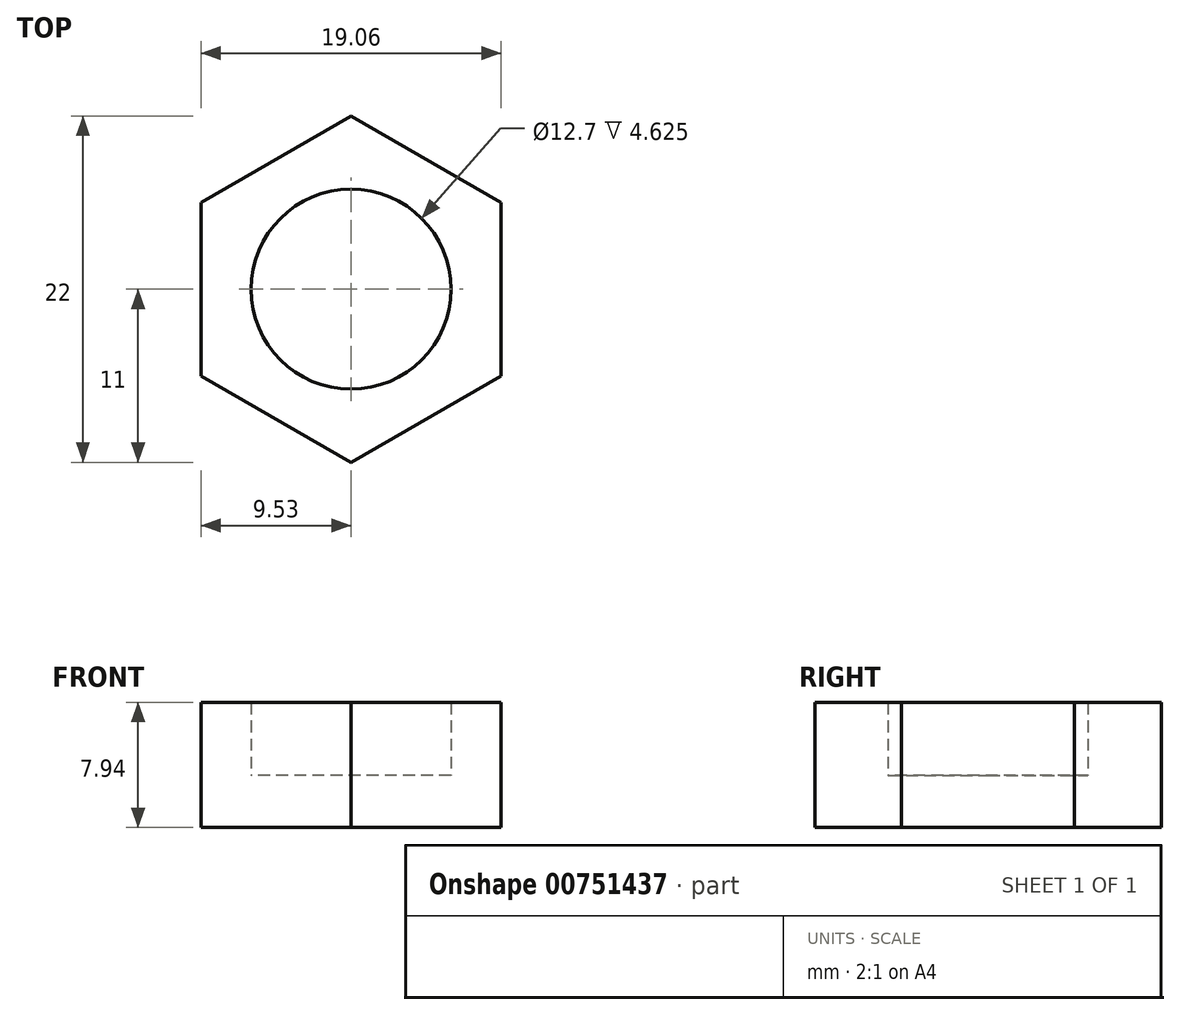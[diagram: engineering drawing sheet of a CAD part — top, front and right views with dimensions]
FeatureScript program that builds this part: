
annotation { "Feature Type Name" : "Feature", "Feature Type Description" : "" }
export const myFeature = defineFeature(function(context is Context, id is Id, definition is map)
    precondition{}
    {
        {
            assignVariable(context, id + "F0", {"name" : "ShaftHeight", "anyValue" : 3});
        }
        {
            var Q0;
            Q0=qCreatedBy(makeId("Top.planeOp"),FACE);
            var sketch = newSketch(context, id + "F1", { "sketchPlane" : qUnion([Q0])});
            skCircle(sketch, "E0.cCircle", {"center": v(0, 0) * mm, "radius": 9.53 * mm, "construction": true});
            skLineSegment(sketch, "E0.0", {"start": v(9.53, 5.5) * mm, "end": v(9.53, -5.5) * mm});
            skLineSegment(sketch, "E0.1", {"start": v(9.53, -5.5) * mm, "end": v(0, -11) * mm});
            skLineSegment(sketch, "E0.2", {"start": v(0, -11) * mm, "end": v(-9.52, -5.5) * mm});
            skLineSegment(sketch, "E0.3", {"start": v(-9.52, -5.5) * mm, "end": v(-9.53, 5.5) * mm});
            skLineSegment(sketch, "E0.4", {"start": v(-9.53, 5.5) * mm, "end": v(0, 11) * mm});
            skLineSegment(sketch, "E0.5", {"start": v(0, 11) * mm, "end": v(9.53, 5.5) * mm});
            skPoint(sketch, "E0.0.midPoint", {"position": v(9.53, 0) * mm});
            skCircle(sketch, "E1", {"center": v(0, 0) * mm, "radius": 6.35 * mm});
            skSolve(sketch);
        }
        {
            var Q0;
            Q0=makeQuery(id+"F1.imprint","IMPRINT",FACE,{"disambiguationData":[TD([[makeQuery(id+"F1.imprint","IMPRINT",EDGE,{"derivedFrom":sQuery(id+"F1.wireOp",EDGE,"E0.0")}),-1.0]])]});
            extrude(context, id + "F2", {"entities" : qUnion([Q0]), "depth" : 7.94 * mm, "offsetDistance" : 25.4 * mm});
        }
        {
            var Q0;
            Q0=makeQuery(id+"F1.imprint","IMPRINT",FACE,{"disambiguationData":[TD([[makeQuery(id+"F1.imprint","IMPRINT",EDGE,{"derivedFrom":sQuery(id+"F1.wireOp",EDGE,"E1")}),1.0]])]});
            extrude(context, id + "F3", {"entities" : qUnion([Q0]), "operationType" : NewBodyOperationType.ADD, "depth" : (getVariable(context, 'ShaftHeight') + 0.31) * mm, "offsetDistance" : 25.4 * mm});
        }
    });
